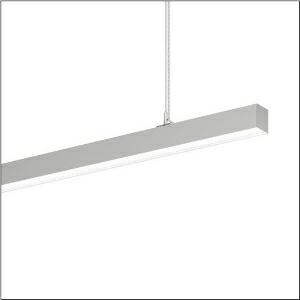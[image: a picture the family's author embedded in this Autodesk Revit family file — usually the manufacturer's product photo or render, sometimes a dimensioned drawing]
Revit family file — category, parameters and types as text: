
# Revit family: silica_r__21_51mx30da44sb_e9ec
name_source: partatom
category: Lighting Fixtures
units: mm (PartAtom-declared; Revit-internal decimal feet)

## family parameters
Cut with Voids When Loaded = No
Host = Face
Light Source = No
Part Type = Normal
Room Calculation Point = No
Round Connector Dimension = Use Diameter
Shared = No

## types (1)
- --- (1 x LED, 4210 lm, 26 W, 4000K)
    Apparent Load = 26 VA
    CIE Flux Codes = 47 79 96 57 100
    Color Rendering = 80
    Color Temperature = 4000K
    Default Elevation = 1800 mm
    Description = Silica® 21, office luminaire, primary optical cover: cover, of PMMA, opal, light emission: direct/indirect distribution, primary light characteristic: symmetric, installation type: suspended mounting, LED, rated luminous flux: 4.210lm, luminous efficacy: 162lm/W, light colour: 840, colour temperature: 4000K, control gear: DALI 2, with terminal, 3+2-pole, max. 2.5mm², mains connection: 220..240V, AC, 50/60Hz, rated input power: 26W, luminaire housing, of aluminium, metallic grey (RAL 9006), length: 1.204mm, width: 53mm, height: 53mm, protection rating (complete): IP20, insulation class (complete): insulation class I (protective earthing), certification: CE, permissible operating ambient temperature: 0..+35°C, standard: EN 50419, packaging unit: 1 piece
    Height = 53 mm
    Lamp = 1 x LED
    Lamp Light Flux = 4210 lm
    Lamp Power = 26 W
    Lamp count = 1
    Length = 1204 mm
    Luminous efficacy = 162 lm/W
    Manufacturer = Siteco
    ModVariant = No
    Model = 51MX30DA44SB
    Mounting Place = Ceiling
    Mounting Type = Pendant
    Number of Poles = 1
    OnlyDefault = Yes
    Power Factor = 1
    Product Name = Silica® 21
    Product group = office luminaire | ceiling pendant
    ProductGroupID = 904
    Protection Class = Protection class I
    Protection Degree = IP 20
    RLX_Detail_Level = 1
    RLX_Emergency_Light_Flux = 0 lm
    RLX_Emergency_Type = 0
    RLX_Emergency_Type_DB = No
    RlxData = <blob elided: 23157 chars, md5=337ce29b>
    Socket = socket
    Standby Power = 0 W
    System Light Flux = 4210 lm
    System Power = 26 W
    Type Comments = factory setting: luminous flux: 100 % | dim-lin: 254 | 218 mA
    Type Image = l_1335864.jpg
    URL = http://relux.com
    VarID = @adj_117186
    Voltage = 0 V
    Weight = 0.00 kg
    Width = 53 mm

## geometry (parser evidence)
native form markers: Blend x4, Sweep x11
no freeform markers — native parametric forms only
